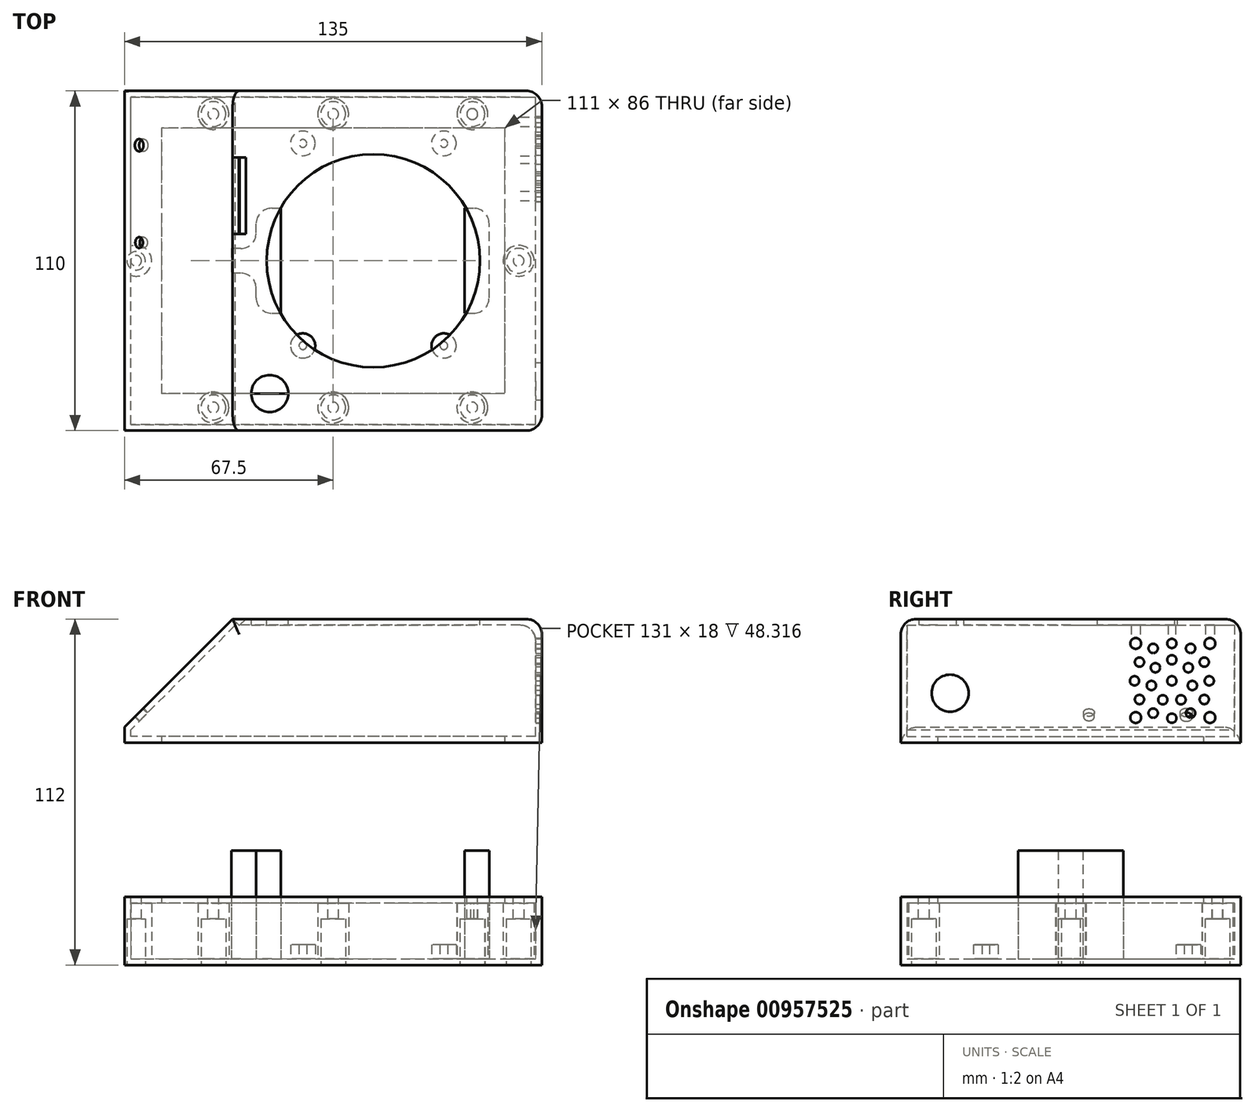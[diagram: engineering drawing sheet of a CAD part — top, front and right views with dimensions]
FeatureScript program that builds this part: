
annotation { "Feature Type Name" : "Feature", "Feature Type Description" : "" }
export const myFeature = defineFeature(function(context is Context, id is Id, definition is map)
    precondition{}
    {
        {
            var Q0;
            Q0=qCreatedBy(makeId("Front.planeOp"),FACE);
            var sketch = newSketch(context, id + "F0", { "sketchPlane" : qUnion([Q0])});
            skLineSegment(sketch, "E0.bottom", {"start": v(67.5, 0) * mm, "end": v(65.5, 0) * mm});
            skLineSegment(sketch, "E0.top", {"start": v(67.5, 40) * mm, "end": v(-32.5, 40) * mm});
            skLineSegment(sketch, "E0.left", {"start": v(67.5, 0) * mm, "end": v(67.5, 40) * mm});
            skLineSegment(sketch, "E0.right", {"start": v(-67.5, 0) * mm, "end": v(-67.5, 5) * mm});
            skLineSegment(sketch, "E1", {"start": v(-32.5, 40) * mm, "end": v(-67.5, 5) * mm});
            skLineSegment(sketch, "E2.0", {"start": v(65.5, 2) * mm, "end": v(65.5, 38) * mm});
            skLineSegment(sketch, "E2.1", {"start": v(65.5, 38) * mm, "end": v(-31.67, 38) * mm});
            skLineSegment(sketch, "E2.2", {"start": v(-31.67, 38) * mm, "end": v(-65.5, 4.17) * mm});
            skLineSegment(sketch, "E2.3", {"start": v(-65.5, 2) * mm, "end": v(-65.5, 4.17) * mm});
            skLineSegment(sketch, "E3.trimOffspring", {"start": v(-65.5, 0) * mm, "end": v(-67.5, 0) * mm});
            skLineSegment(sketch, "E4.bottom", {"start": v(-65.5, 0) * mm, "end": v(-55.5, 0) * mm});
            skLineSegment(sketch, "E4.top", {"start": v(-65.5, 2) * mm, "end": v(-55.5, 2) * mm});
            skLineSegment(sketch, "E4.right", {"start": v(-55.5, 0) * mm, "end": v(-55.5, 2) * mm});
            skLineSegment(sketch, "E5.bottom", {"start": v(65.5, 0) * mm, "end": v(55.5, 0) * mm});
            skLineSegment(sketch, "E5.top", {"start": v(65.5, 2) * mm, "end": v(55.5, 2) * mm});
            skLineSegment(sketch, "E5.right", {"start": v(55.5, 0) * mm, "end": v(55.5, 2) * mm});
            skSolve(sketch);
        }
        {
            var Q0;
            Q0=makeQuery(id+"F0.imprint","IMPRINT",FACE,{"disambiguationData":[TD([[makeQuery(id+"F0.imprint","IMPRINT",EDGE,{"derivedFrom":sQuery(id+"F0.wireOp",EDGE,"E0.bottom")}),-1.0]])]});
            extrude(context, id + "F1", {"entities" : qUnion([Q0]), "depth" : 55 * mm, "offsetDistance" : 25 * mm, "hasSecondDirection" : true, "secondDirectionOppositeDirection" : true, "secondDirectionDepth" : 55 * mm});
        }
        {
            var Q0;
            Q0=makeQuery(id+"F1.opExtrude","SWEPT_FACE",FACE,{"disambiguationData":[OSD([sQuery(id+"F0.wireOp",EDGE,"E0.top")])]});
            var sketch = newSketch(context, id + "F2", { "sketchPlane" : qUnion([Q0])});
            skCircle(sketch, "E6", {"center": v(13, 0) * mm, "radius": 34.5 * mm});
            skCircle(sketch, "E7", {"center": v(-20.5, -43) * mm, "radius": 6 * mm});
            skSolve(sketch);
        }
        {
            var Q0;
            Q0 = qSketchRegion(id + "F2", true);
            extrude(context, id + "F3", {"entities" : qUnion([Q0]), "operationType" : NewBodyOperationType.REMOVE, "oppositeDirection" : true, "depth" : 3 * mm, "offsetDistance" : 25 * mm});
        }
        {
            var Q0;
            Q0=makeQuery(id+"F1.opExtrude","CAP_FACE",FACE,{"disambiguationData":[OSD([sQuery(id+"F0.wireOp",EDGE,"E0.bottom"),sQuery(id+"F0.wireOp",EDGE,"E0.top"),sQuery(id+"F0.wireOp",EDGE,"E0.left"),sQuery(id+"F0.wireOp",EDGE,"E0.right"),sQuery(id+"F0.wireOp",EDGE,"E1"),sQuery(id+"F0.wireOp",EDGE,"E2.0"),sQuery(id+"F0.wireOp",EDGE,"E2.1"),sQuery(id+"F0.wireOp",EDGE,"E2.2"),sQuery(id+"F0.wireOp",EDGE,"E2.3"),sQuery(id+"F0.wireOp",EDGE,"E3.trimOffspring"),sQuery(id+"F0.wireOp",EDGE,"E4.bottom"),sQuery(id+"F0.wireOp",EDGE,"E4.top"),sQuery(id+"F0.wireOp",EDGE,"E4.right"),sQuery(id+"F0.wireOp",EDGE,"E5.bottom"),sQuery(id+"F0.wireOp",EDGE,"E5.top"),sQuery(id+"F0.wireOp",EDGE,"E5.right")])],"isStart":false});
            var sketch = newSketch(context, id + "F4", { "sketchPlane" : qUnion([Q0])});
            skLineSegment(sketch, "E8.0", {"start": v(55.5, 0) * mm, "end": v(55.5, 2) * mm});
            skLineSegment(sketch, "E8.1", {"start": v(65.5, 2) * mm, "end": v(55.5, 2) * mm});
            skLineSegment(sketch, "E8.2", {"start": v(65.5, 2) * mm, "end": v(65.5, 38) * mm});
            skLineSegment(sketch, "E8.3", {"start": v(65.5, 38) * mm, "end": v(-31.67, 38) * mm});
            skLineSegment(sketch, "E8.4", {"start": v(-31.67, 38) * mm, "end": v(-65.5, 4.17) * mm});
            skLineSegment(sketch, "E8.5", {"start": v(-55.5, 0) * mm, "end": v(-55.5, 2) * mm});
            skLineSegment(sketch, "E8.6", {"start": v(-65.5, 2) * mm, "end": v(-55.5, 2) * mm});
            skLineSegment(sketch, "E8.7", {"start": v(-65.5, 2) * mm, "end": v(-65.5, 4.17) * mm});
            skLineSegment(sketch, "E9", {"start": v(-55.5, 0) * mm, "end": v(55.5, 0) * mm});
            skSolve(sketch);
        }
        {
            var Q0;
            Q0 = qSketchRegion(id + "F4", true);
            extrude(context, id + "F5", {"entities" : qUnion([Q0]), "operationType" : NewBodyOperationType.ADD, "oppositeDirection" : true, "depth" : 2 * mm, "offsetDistance" : 25 * mm});
        }
        {
            var Q0;
            Q0=makeQuery(id+"F4.imprint","IMPRINT",FACE,{"disambiguationData":[TD([[makeQuery(id+"F4.imprint","IMPRINT",EDGE,{"derivedFrom":sQuery(id+"F4.wireOp",EDGE,"E8.0")}),1.0]])]});
            extrude(context, id + "F6", {"entities" : qUnion([Q0]), "operationType" : NewBodyOperationType.ADD, "oppositeDirection" : true, "depth" : 2 * mm, "offsetDistance" : 25 * mm});
        }
        {
            var Q0;
            Q0=makeQuery(id+"F1.opExtrude","CAP_FACE",FACE,{"disambiguationData":[OSD([sQuery(id+"F0.wireOp",EDGE,"E0.bottom"),sQuery(id+"F0.wireOp",EDGE,"E0.top"),sQuery(id+"F0.wireOp",EDGE,"E0.left"),sQuery(id+"F0.wireOp",EDGE,"E0.right"),sQuery(id+"F0.wireOp",EDGE,"E1"),sQuery(id+"F0.wireOp",EDGE,"E2.0"),sQuery(id+"F0.wireOp",EDGE,"E2.1"),sQuery(id+"F0.wireOp",EDGE,"E2.2"),sQuery(id+"F0.wireOp",EDGE,"E2.3"),sQuery(id+"F0.wireOp",EDGE,"E3.trimOffspring"),sQuery(id+"F0.wireOp",EDGE,"E4.bottom"),sQuery(id+"F0.wireOp",EDGE,"E4.top"),sQuery(id+"F0.wireOp",EDGE,"E4.right"),sQuery(id+"F0.wireOp",EDGE,"E5.bottom"),sQuery(id+"F0.wireOp",EDGE,"E5.top"),sQuery(id+"F0.wireOp",EDGE,"E5.right")])],"isStart":true});
            var sketch = newSketch(context, id + "F7", { "sketchPlane" : qUnion([Q0])});
            skLineSegment(sketch, "E10.0.0", {"start": v(55.5, 0) * mm, "end": v(55.5, 2) * mm});
            skLineSegment(sketch, "E10.0.1", {"start": v(55.5, 2) * mm, "end": v(65.5, 2) * mm});
            skLineSegment(sketch, "E10.0.2", {"start": v(65.5, 2) * mm, "end": v(65.5, 4.17) * mm});
            skLineSegment(sketch, "E10.0.3", {"start": v(65.5, 4.17) * mm, "end": v(31.67, 38) * mm});
            skLineSegment(sketch, "E10.0.4", {"start": v(31.67, 38) * mm, "end": v(-65.5, 38) * mm});
            skLineSegment(sketch, "E10.0.5", {"start": v(-65.5, 38) * mm, "end": v(-65.5, 2) * mm});
            skLineSegment(sketch, "E10.0.6", {"start": v(-65.5, 2) * mm, "end": v(-55.5, 2) * mm});
            skLineSegment(sketch, "E10.0.7", {"start": v(-55.5, 2) * mm, "end": v(-55.5, 0) * mm});
            skLineSegment(sketch, "E10.0.8", {"start": v(-55.5, 0) * mm, "end": v(55.5, 0) * mm});
            skSolve(sketch);
        }
        {
            var Q0;
            Q0=makeQuery(id+"F7.imprint","IMPRINT",FACE,{"disambiguationData":[TD([[makeQuery(id+"F7.imprint","IMPRINT",EDGE,{"derivedFrom":sQuery(id+"F7.wireOp",EDGE,"E10.0.0")}),1.0]])]});
            extrude(context, id + "F8", {"entities" : qUnion([Q0]), "operationType" : NewBodyOperationType.ADD, "oppositeDirection" : true, "depth" : 2 * mm, "offsetDistance" : 25 * mm});
        }
        {
            var Q0;
            Q0=makeQuery(id+"F1.opExtrude","SWEPT_FACE",FACE,{"disambiguationData":[OSD([sQuery(id+"F0.wireOp",EDGE,"E1")])]});
            var sketch = newSketch(context, id + "F9", { "sketchPlane" : qUnion([Q0])});
            skLineSegment(sketch, "E11.bottom", {"start": v(-8.7, 35.7) * mm, "end": v(-33.5, 35.7) * mm});
            skLineSegment(sketch, "E11.top", {"start": v(-8.7, -35.7) * mm, "end": v(-33.5, -35.7) * mm});
            skLineSegment(sketch, "E11.left", {"start": v(-8.7, 35.7) * mm, "end": v(-8.7, -35.7) * mm});
            skLineSegment(sketch, "E11.right", {"start": v(-33.5, 35.7) * mm, "end": v(-33.5, -35.7) * mm});
            skLineSegment(sketch, "E12.bottom", {"start": v(-5.9, 37.5) * mm, "end": v(-37.4, 37.5) * mm, "construction": true});
            skLineSegment(sketch, "E12.top", {"start": v(-5.9, -37.5) * mm, "end": v(-37.4, -37.5) * mm, "construction": true});
            skLineSegment(sketch, "E12.left", {"start": v(-5.9, 37.5) * mm, "end": v(-5.9, -37.5) * mm, "construction": true});
            skLineSegment(sketch, "E12.right", {"start": v(-37.4, 37.5) * mm, "end": v(-37.4, -37.5) * mm, "construction": true});
            skCircle(sketch, "E13", {"center": v(-37.4, -37.5) * mm, "radius": 2 * mm});
            skCircle(sketch, "E14", {"center": v(-37.4, 37.5) * mm, "radius": 2 * mm});
            skCircle(sketch, "E15", {"center": v(-5.9, 37.5) * mm, "radius": 1.75 * mm});
            skCircle(sketch, "E16", {"center": v(-5.9, -37.5) * mm, "radius": 1.75 * mm});
            skSolve(sketch);
        }
        {
            var Q0;
            Q0=makeQuery(id+"F9.imprint","IMPRINT",FACE,{"disambiguationData":[TD([[makeQuery(id+"F9.imprint","IMPRINT",EDGE,{"derivedFrom":sQuery(id+"F9.wireOp",EDGE,"E11.bottom")}),1.0]])]});
            var Q1;
            Q1=makeQuery(id+"F9.imprint","IMPRINT",FACE,{"disambiguationData":[TD([[makeQuery(id+"F9.imprint","IMPRINT",EDGE,{"derivedFrom":sQuery(id+"F9.wireOp",EDGE,"E15")}),1.0]])]});
            var Q2;
            Q2=makeQuery(id+"F9.imprint","IMPRINT",FACE,{"disambiguationData":[TD([[makeQuery(id+"F9.imprint","IMPRINT",EDGE,{"derivedFrom":sQuery(id+"F9.wireOp",EDGE,"E14")}),1.0]])]});
            var Q3;
            Q3=makeQuery(id+"F9.imprint","IMPRINT",FACE,{"disambiguationData":[TD([[makeQuery(id+"F9.imprint","IMPRINT",EDGE,{"derivedFrom":sQuery(id+"F9.wireOp",EDGE,"E13")}),1.0]])]});
            var Q4;
            Q4=makeQuery(id+"F9.imprint","IMPRINT",FACE,{"disambiguationData":[TD([[makeQuery(id+"F9.imprint","IMPRINT",EDGE,{"derivedFrom":sQuery(id+"F9.wireOp",EDGE,"E16")}),1.0]])]});
            extrude(context, id + "F10", {"entities" : qUnion([Q0, Q1, Q2, Q3, Q4]), "operationType" : NewBodyOperationType.REMOVE, "oppositeDirection" : true, "depth" : 3 * mm, "offsetDistance" : 25 * mm});
        }
        {
            var Q0;
            Q0=qCreatedBy(makeId("Top.planeOp"),FACE);
            var sketch = newSketch(context, id + "F11", { "sketchPlane" : qUnion([Q0])});
            skLineSegment(sketch, "E17.0", {"start": v(55.5, -53) * mm, "end": v(55.5, -43) * mm});
            skLineSegment(sketch, "E17.1", {"start": v(55.5, 53) * mm, "end": v(-55.5, 53) * mm});
            skLineSegment(sketch, "E17.2", {"start": v(-55.5, -53) * mm, "end": v(-55.5, -43) * mm});
            skLineSegment(sketch, "E17.3", {"start": v(-55.5, -53) * mm, "end": v(55.5, -53) * mm});
            skLineSegment(sketch, "E18", {"start": v(55.5, 43) * mm, "end": v(-55.5, 43) * mm});
            skLineSegment(sketch, "E19", {"start": v(55.5, -43) * mm, "end": v(-55.5, -43) * mm});
            skLineSegment(sketch, "E20.trimOffspring", {"start": v(-55.5, 43) * mm, "end": v(-55.5, 53) * mm});
            skLineSegment(sketch, "E21.trimOffspring", {"start": v(55.5, 43) * mm, "end": v(55.5, 53) * mm});
            skSolve(sketch);
        }
        {
            var Q0;
            Q0=makeQuery(id+"F11.imprint","IMPRINT",FACE,{"disambiguationData":[TD([[makeQuery(id+"F11.imprint","IMPRINT",EDGE,{"derivedFrom":sQuery(id+"F11.wireOp",EDGE,"E17.1")}),1.0]])]});
            var Q1;
            Q1=makeQuery(id+"F11.imprint","IMPRINT",FACE,{"disambiguationData":[TD([[makeQuery(id+"F11.imprint","IMPRINT",EDGE,{"derivedFrom":sQuery(id+"F11.wireOp",EDGE,"E17.0")}),1.0]])]});
            extrude(context, id + "F12", {"entities" : qUnion([Q0, Q1]), "operationType" : NewBodyOperationType.ADD, "depth" : 2 * mm, "offsetDistance" : 25 * mm});
        }
        {
            var Q0;
            Q0=makeQuery(id+"F1.opExtrude","SWEPT_FACE",FACE,{"disambiguationData":[OSD([sQuery(id+"F0.wireOp",EDGE,"E0.left")])]});
            var sketch = newSketch(context, id + "F13", { "sketchPlane" : qUnion([Q0])});
            skCircle(sketch, "E22", {"center": v(-39, 16) * mm, "radius": 6 * mm});
            skPoint(sketch, "E23.centerSnap0", {"position": v(55, 20) * mm});
            skLineSegment(sketch, "E24.bottom", {"start": v(21.03, 32.1) * mm, "end": v(45.03, 32.1) * mm, "construction": true});
            skLineSegment(sketch, "E24.top", {"start": v(21.03, 8.1) * mm, "end": v(45.03, 8.1) * mm, "construction": true});
            skLineSegment(sketch, "E24.left", {"start": v(21.03, 32.1) * mm, "end": v(21.03, 8.1) * mm, "construction": true});
            skLineSegment(sketch, "E24.right", {"start": v(45.03, 32.1) * mm, "end": v(45.03, 8.1) * mm, "construction": true});
            skCircle(sketch, "E25", {"center": v(21.03, 32.1) * mm, "radius": 1.75 * mm});
            skCircle(sketch, "E26", {"center": v(45.03, 32.1) * mm, "radius": 1.75 * mm});
            skCircle(sketch, "E27", {"center": v(45.03, 8.1) * mm, "radius": 1.75 * mm});
            skCircle(sketch, "E28", {"center": v(21.03, 8.1) * mm, "radius": 1.75 * mm});
            skPoint(sketch, "E29.center.orphan", {"position": v(45.03, 27.1) * mm});
            skCircle(sketch, "E30", {"center": v(32.73, 20) * mm, "radius": 14.2 * mm, "construction": true});
            skCircle(sketch, "E31.cCircle", {"center": v(32.73, 20) * mm, "radius": 12.1 * mm, "construction": true});
            skLineSegment(sketch, "E31.0", {"start": v(32.73, 32.1) * mm, "end": v(38.78, 30.48) * mm, "construction": true});
            skLineSegment(sketch, "E31.1", {"start": v(38.78, 30.48) * mm, "end": v(43.2, 26.05) * mm, "construction": true});
            skLineSegment(sketch, "E31.2", {"start": v(43.2, 26.05) * mm, "end": v(44.83, 20) * mm, "construction": true});
            skLineSegment(sketch, "E31.3", {"start": v(44.83, 20) * mm, "end": v(43.2, 13.95) * mm, "construction": true});
            skLineSegment(sketch, "E31.4", {"start": v(43.2, 13.95) * mm, "end": v(38.78, 9.52) * mm, "construction": true});
            skLineSegment(sketch, "E31.5", {"start": v(38.78, 9.52) * mm, "end": v(32.73, 7.9) * mm, "construction": true});
            skLineSegment(sketch, "E31.6", {"start": v(32.73, 7.9) * mm, "end": v(26.68, 9.52) * mm, "construction": true});
            skLineSegment(sketch, "E31.7", {"start": v(26.68, 9.52) * mm, "end": v(22.25, 13.95) * mm, "construction": true});
            skLineSegment(sketch, "E31.8", {"start": v(22.25, 13.95) * mm, "end": v(20.63, 20) * mm, "construction": true});
            skLineSegment(sketch, "E31.9", {"start": v(20.63, 20) * mm, "end": v(22.25, 26.05) * mm, "construction": true});
            skLineSegment(sketch, "E31.10", {"start": v(22.25, 26.05) * mm, "end": v(26.68, 30.48) * mm, "construction": true});
            skLineSegment(sketch, "E31.11", {"start": v(26.68, 30.48) * mm, "end": v(32.73, 32.1) * mm, "construction": true});
            skCircle(sketch, "E32", {"center": v(32.73, 32.1) * mm, "radius": 1.5 * mm});
            skCircle(sketch, "E33", {"center": v(38.78, 30.48) * mm, "radius": 1.5 * mm});
            skCircle(sketch, "E34", {"center": v(43.2, 26.05) * mm, "radius": 1.5 * mm});
            skCircle(sketch, "E35", {"center": v(26.68, 30.48) * mm, "radius": 1.5 * mm});
            skCircle(sketch, "E36", {"center": v(22.25, 26.05) * mm, "radius": 1.5 * mm});
            skCircle(sketch, "E37", {"center": v(44.83, 20) * mm, "radius": 1.5 * mm});
            skCircle(sketch, "E38", {"center": v(43.2, 13.95) * mm, "radius": 1.5 * mm});
            skCircle(sketch, "E39", {"center": v(38.78, 9.52) * mm, "radius": 1.5 * mm});
            skCircle(sketch, "E40", {"center": v(32.73, 7.9) * mm, "radius": 1.5 * mm});
            skCircle(sketch, "E41", {"center": v(26.68, 9.52) * mm, "radius": 1.5 * mm});
            skCircle(sketch, "E42", {"center": v(22.25, 13.95) * mm, "radius": 1.5 * mm});
            skCircle(sketch, "E43", {"center": v(20.63, 20) * mm, "radius": 1.5 * mm});
            skCircle(sketch, "E44.cCircle", {"center": v(32.73, 20) * mm, "radius": 6.8 * mm, "construction": true});
            skLineSegment(sketch, "E44.0", {"start": v(32.73, 26.8) * mm, "end": v(38.04, 24.24) * mm, "construction": true});
            skLineSegment(sketch, "E44.1", {"start": v(38.04, 24.24) * mm, "end": v(39.36, 18.49) * mm, "construction": true});
            skLineSegment(sketch, "E44.2", {"start": v(39.36, 18.49) * mm, "end": v(35.68, 13.87) * mm, "construction": true});
            skLineSegment(sketch, "E44.3", {"start": v(35.68, 13.87) * mm, "end": v(29.78, 13.87) * mm, "construction": true});
            skLineSegment(sketch, "E44.4", {"start": v(29.78, 13.87) * mm, "end": v(26.1, 18.49) * mm, "construction": true});
            skLineSegment(sketch, "E44.5", {"start": v(26.1, 18.49) * mm, "end": v(27.41, 24.24) * mm, "construction": true});
            skLineSegment(sketch, "E44.6", {"start": v(27.41, 24.24) * mm, "end": v(32.73, 26.8) * mm, "construction": true});
            skCircle(sketch, "E45", {"center": v(32.73, 26.8) * mm, "radius": 1.5 * mm});
            skCircle(sketch, "E46", {"center": v(38.04, 24.24) * mm, "radius": 1.5 * mm});
            skCircle(sketch, "E47", {"center": v(39.36, 18.49) * mm, "radius": 1.5 * mm});
            skCircle(sketch, "E48", {"center": v(35.68, 13.87) * mm, "radius": 1.5 * mm});
            skCircle(sketch, "E49", {"center": v(29.78, 13.87) * mm, "radius": 1.5 * mm});
            skCircle(sketch, "E50", {"center": v(26.1, 18.49) * mm, "radius": 1.5 * mm});
            skCircle(sketch, "E51", {"center": v(27.41, 24.24) * mm, "radius": 1.5 * mm});
            skCircle(sketch, "E52", {"center": v(32.73, 20) * mm, "radius": 1.5 * mm});
            skSolve(sketch);
        }
        {
            var Q0;
            Q0=makeQuery(id+"F13.imprint","IMPRINT",FACE,{"disambiguationData":[TD([[makeQuery(id+"F13.imprint","IMPRINT",EDGE,{"derivedFrom":sQuery(id+"F13.wireOp",EDGE,"E22")}),1.0]])]});
            var Q1;
            Q1=makeQuery(id+"F13.imprint","IMPRINT",FACE,{"disambiguationData":[TD([[makeQuery(id+"F13.imprint","IMPRINT",EDGE,{"derivedFrom":sQuery(id+"F13.wireOp",EDGE,"E28")}),1.0]])]});
            var Q2;
            Q2=makeQuery(id+"F13.imprint","IMPRINT",FACE,{"disambiguationData":[TD([[makeQuery(id+"F13.imprint","IMPRINT",EDGE,{"derivedFrom":sQuery(id+"F13.wireOp",EDGE,"E41")}),1.0]])]});
            var Q3;
            Q3=makeQuery(id+"F13.imprint","IMPRINT",FACE,{"disambiguationData":[TD([[makeQuery(id+"F13.imprint","IMPRINT",EDGE,{"derivedFrom":sQuery(id+"F13.wireOp",EDGE,"E42")}),1.0]])]});
            var Q4;
            Q4=makeQuery(id+"F13.imprint","IMPRINT",FACE,{"disambiguationData":[TD([[makeQuery(id+"F13.imprint","IMPRINT",EDGE,{"derivedFrom":sQuery(id+"F13.wireOp",EDGE,"E43")}),1.0]])]});
            var Q5;
            Q5=makeQuery(id+"F13.imprint","IMPRINT",FACE,{"disambiguationData":[TD([[makeQuery(id+"F13.imprint","IMPRINT",EDGE,{"derivedFrom":sQuery(id+"F13.wireOp",EDGE,"E50")}),1.0]])]});
            var Q6;
            Q6=makeQuery(id+"F13.imprint","IMPRINT",FACE,{"disambiguationData":[TD([[makeQuery(id+"F13.imprint","IMPRINT",EDGE,{"derivedFrom":sQuery(id+"F13.wireOp",EDGE,"E51")}),1.0]])]});
            var Q7;
            Q7=makeQuery(id+"F13.imprint","IMPRINT",FACE,{"disambiguationData":[TD([[makeQuery(id+"F13.imprint","IMPRINT",EDGE,{"derivedFrom":sQuery(id+"F13.wireOp",EDGE,"E36")}),1.0]])]});
            var Q8;
            Q8=makeQuery(id+"F13.imprint","IMPRINT",FACE,{"disambiguationData":[TD([[makeQuery(id+"F13.imprint","IMPRINT",EDGE,{"derivedFrom":sQuery(id+"F13.wireOp",EDGE,"E35")}),1.0]])]});
            var Q9;
            Q9=makeQuery(id+"F13.imprint","IMPRINT",FACE,{"disambiguationData":[TD([[makeQuery(id+"F13.imprint","IMPRINT",EDGE,{"derivedFrom":sQuery(id+"F13.wireOp",EDGE,"E32")}),1.0]])]});
            var Q10;
            Q10=makeQuery(id+"F13.imprint","IMPRINT",FACE,{"disambiguationData":[TD([[makeQuery(id+"F13.imprint","IMPRINT",EDGE,{"derivedFrom":sQuery(id+"F13.wireOp",EDGE,"E25")}),1.0]])]});
            var Q11;
            Q11=makeQuery(id+"F13.imprint","IMPRINT",FACE,{"disambiguationData":[TD([[makeQuery(id+"F13.imprint","IMPRINT",EDGE,{"derivedFrom":sQuery(id+"F13.wireOp",EDGE,"E33")}),1.0]])]});
            var Q12;
            Q12=makeQuery(id+"F13.imprint","IMPRINT",FACE,{"disambiguationData":[TD([[makeQuery(id+"F13.imprint","IMPRINT",EDGE,{"derivedFrom":sQuery(id+"F13.wireOp",EDGE,"E45")}),1.0]])]});
            var Q13;
            Q13=makeQuery(id+"F13.imprint","IMPRINT",FACE,{"disambiguationData":[TD([[makeQuery(id+"F13.imprint","IMPRINT",EDGE,{"derivedFrom":sQuery(id+"F13.wireOp",EDGE,"E52")}),1.0]])]});
            var Q14;
            Q14=makeQuery(id+"F13.imprint","IMPRINT",FACE,{"disambiguationData":[TD([[makeQuery(id+"F13.imprint","IMPRINT",EDGE,{"derivedFrom":sQuery(id+"F13.wireOp",EDGE,"E48")}),1.0]])]});
            var Q15;
            Q15=makeQuery(id+"F13.imprint","IMPRINT",FACE,{"disambiguationData":[TD([[makeQuery(id+"F13.imprint","IMPRINT",EDGE,{"derivedFrom":sQuery(id+"F13.wireOp",EDGE,"E47")}),1.0]])]});
            var Q16;
            Q16=makeQuery(id+"F13.imprint","IMPRINT",FACE,{"disambiguationData":[TD([[makeQuery(id+"F13.imprint","IMPRINT",EDGE,{"derivedFrom":sQuery(id+"F13.wireOp",EDGE,"E46")}),1.0]])]});
            var Q17;
            Q17=makeQuery(id+"F13.imprint","IMPRINT",FACE,{"disambiguationData":[TD([[makeQuery(id+"F13.imprint","IMPRINT",EDGE,{"derivedFrom":sQuery(id+"F13.wireOp",EDGE,"E34")}),1.0]])]});
            var Q18;
            Q18=makeQuery(id+"F13.imprint","IMPRINT",FACE,{"disambiguationData":[TD([[makeQuery(id+"F13.imprint","IMPRINT",EDGE,{"derivedFrom":sQuery(id+"F13.wireOp",EDGE,"E26")}),1.0]])]});
            var Q19;
            Q19=makeQuery(id+"F13.imprint","IMPRINT",FACE,{"disambiguationData":[TD([[makeQuery(id+"F13.imprint","IMPRINT",EDGE,{"derivedFrom":sQuery(id+"F13.wireOp",EDGE,"E37")}),1.0]])]});
            var Q20;
            Q20=makeQuery(id+"F13.imprint","IMPRINT",FACE,{"disambiguationData":[TD([[makeQuery(id+"F13.imprint","IMPRINT",EDGE,{"derivedFrom":sQuery(id+"F13.wireOp",EDGE,"E38")}),1.0]])]});
            var Q21;
            Q21=makeQuery(id+"F13.imprint","IMPRINT",FACE,{"disambiguationData":[TD([[makeQuery(id+"F13.imprint","IMPRINT",EDGE,{"derivedFrom":sQuery(id+"F13.wireOp",EDGE,"E27")}),1.0]])]});
            var Q22;
            Q22=makeQuery(id+"F13.imprint","IMPRINT",FACE,{"disambiguationData":[TD([[makeQuery(id+"F13.imprint","IMPRINT",EDGE,{"derivedFrom":sQuery(id+"F13.wireOp",EDGE,"E39")}),1.0]])]});
            var Q23;
            Q23=makeQuery(id+"F13.imprint","IMPRINT",FACE,{"disambiguationData":[TD([[makeQuery(id+"F13.imprint","IMPRINT",EDGE,{"derivedFrom":sQuery(id+"F13.wireOp",EDGE,"E40")}),1.0]])]});
            var Q24;
            Q24=makeQuery(id+"F13.imprint","IMPRINT",FACE,{"disambiguationData":[TD([[makeQuery(id+"F13.imprint","IMPRINT",EDGE,{"derivedFrom":sQuery(id+"F13.wireOp",EDGE,"E49")}),1.0]])]});
            extrude(context, id + "F14", {"entities" : qUnion([Q0, Q1, Q2, Q3, Q4, Q5, Q6, Q7, Q8, Q9, Q10, Q11, Q12, Q13, Q14, Q15, Q16, Q17, Q18, Q19, Q20, Q21, Q22, Q23, Q24]), "operationType" : NewBodyOperationType.REMOVE, "oppositeDirection" : true, "depth" : 3 * mm, "offsetDistance" : 25 * mm});
        }
        {
            var Q0;
            Q0=makeQuery(id+"F12.boolean.opBoolean","MERGE",FACE,{"derivedFrom":[makeQuery(id+"F8.boolean.opBoolean","MERGE",FACE,{"derivedFrom":[makeQuery(id+"F5.boolean.opBoolean","MERGE",FACE,{"derivedFrom":[makeQuery(id+"F1.opExtrude","SWEPT_FACE",FACE,{"disambiguationData":[OSD([sQuery(id+"F0.wireOp",EDGE,"E0.bottom"),sQuery(id+"F0.wireOp",EDGE,"E5.bottom")])]}),makeQuery(id+"F1.opExtrude","SWEPT_FACE",FACE,{"disambiguationData":[OSD([sQuery(id+"F0.wireOp",EDGE,"E3.trimOffspring"),sQuery(id+"F0.wireOp",EDGE,"E4.bottom")])]}),makeQuery(id+"F5.opExtrude","SWEPT_FACE",FACE,{"disambiguationData":[OSD([sQuery(id+"F4.wireOp",EDGE,"E9")])]})]}),makeQuery(id+"F8.opExtrude","SWEPT_FACE",FACE,{"disambiguationData":[OSD([sQuery(id+"F7.wireOp",EDGE,"E10.0.8")])]})]}),makeQuery(id+"F12.opExtrude","CAP_FACE",FACE,{"disambiguationData":[OSD([sQuery(id+"F11.wireOp",EDGE,"E17.0"),sQuery(id+"F11.wireOp",EDGE,"E17.2"),sQuery(id+"F11.wireOp",EDGE,"E17.3"),sQuery(id+"F11.wireOp",EDGE,"E19")])],"isStart":true}),makeQuery(id+"F12.opExtrude","CAP_FACE",FACE,{"disambiguationData":[OSD([sQuery(id+"F11.wireOp",EDGE,"E17.1"),sQuery(id+"F11.wireOp",EDGE,"E18"),sQuery(id+"F11.wireOp",EDGE,"E20.trimOffspring"),sQuery(id+"F11.wireOp",EDGE,"E21.trimOffspring")])],"isStart":true})]});
            var sketch = newSketch(context, id + "F15", { "sketchPlane" : qUnion([Q0])});
            skCircle(sketch, "E53", {"center": v(-38.75, 47.5) * mm, "radius": 1.75 * mm});
            skLineSegment(sketch, "E54", {"start": v(-73.28, 47.5) * mm, "end": v(68.94, 47.5) * mm, "construction": true});
            skLineSegment(sketch, "E55", {"start": v(-77.78, -47.5) * mm, "end": v(72.72, -47.5) * mm, "construction": true});
            skLineSegment(sketch, "E56", {"start": v(60, 71.35) * mm, "end": v(60, -59.65) * mm, "construction": true});
            skLineSegment(sketch, "E57", {"start": v(-63.75, 71.72) * mm, "end": v(-63.75, -59.28) * mm, "construction": true});
            skCircle(sketch, "E58", {"center": v(45, 47.5) * mm, "radius": 1.75 * mm});
            skCircle(sketch, "E59", {"center": v(0, 47.5) * mm, "radius": 1.75 * mm});
            skCircle(sketch, "E60", {"center": v(-38.75, -47.5) * mm, "radius": 1.75 * mm});
            skCircle(sketch, "E61", {"center": v(0, -47.5) * mm, "radius": 1.75 * mm});
            skCircle(sketch, "E62", {"center": v(45, -47.5) * mm, "radius": 1.75 * mm});
            skCircle(sketch, "E63", {"center": v(-63.75, 0) * mm, "radius": 1.75 * mm});
            skCircle(sketch, "E64", {"center": v(60, 0) * mm, "radius": 1.75 * mm});
            skSolve(sketch);
        }
        {
            var Q0;
            Q0=makeQuery(id+"F1.opExtrude","CAP_EDGE",EDGE,{"disambiguationData":[OSD([sQuery(id+"F0.wireOp",EDGE,"E0.top")])],"isStart":false});
            var Q1;
            Q1=makeQuery(id+"F5.opExtrude","CAP_EDGE",EDGE,{"disambiguationData":[OSD([sQuery(id+"F4.wireOp",EDGE,"E8.3")])],"isStart":false});
            var Q2;
            Q2=makeQuery(id+"F5.opExtrude","CAP_EDGE",EDGE,{"disambiguationData":[OSD([sQuery(id+"F4.wireOp",EDGE,"E8.4")])],"isStart":false});
            var Q3;
            Q3=makeQuery(id+"F8.opExtrude","CAP_EDGE",EDGE,{"disambiguationData":[OSD([sQuery(id+"F7.wireOp",EDGE,"E10.0.4")])],"isStart":false});
            var Q4;
            Q4=makeQuery(id+"F8.opExtrude","CAP_EDGE",EDGE,{"disambiguationData":[OSD([sQuery(id+"F7.wireOp",EDGE,"E10.0.3")])],"isStart":false});
            var Q5;
            Q5=makeQuery(id+"F1.opExtrude","SWEPT_EDGE",EDGE,{"disambiguationData":[OSD([sQuery(id+"F0.wireOp",EDGE,"E2.0"),sQuery(id+"F0.wireOp",EDGE,"E2.1")])]});
            var Q6;
            Q6=makeQuery(id+"F8.opExtrude","CAP_EDGE",EDGE,{"disambiguationData":[OSD([sQuery(id+"F7.wireOp",EDGE,"E10.0.5")])],"isStart":false});
            var Q7;
            Q7=makeQuery(id+"F5.opExtrude","CAP_EDGE",EDGE,{"disambiguationData":[OSD([sQuery(id+"F4.wireOp",EDGE,"E8.2")])],"isStart":false});
            var Q8;
            Q8=makeQuery(id+"F1.opExtrude","CAP_EDGE",EDGE,{"disambiguationData":[OSD([sQuery(id+"F0.wireOp",EDGE,"E0.left")])],"isStart":true});
            var Q9;
            Q9=makeQuery(id+"F1.opExtrude","SWEPT_EDGE",EDGE,{"disambiguationData":[OSD([sQuery(id+"F0.wireOp",EDGE,"E0.top"),sQuery(id+"F0.wireOp",EDGE,"E0.left")])]});
            var Q10;
            Q10=makeQuery(id+"F1.opExtrude","CAP_EDGE",EDGE,{"disambiguationData":[OSD([sQuery(id+"F0.wireOp",EDGE,"E0.top")])],"isStart":true});
            var Q11;
            Q11=makeQuery(id+"F1.opExtrude","CAP_EDGE",EDGE,{"disambiguationData":[OSD([sQuery(id+"F0.wireOp",EDGE,"E0.left")])],"isStart":false});
            var Q12;
            Q12=makeQuery(id+"F1.opExtrude","CAP_EDGE",EDGE,{"disambiguationData":[OSD([sQuery(id+"F0.wireOp",EDGE,"E1")])],"isStart":false});
            var Q13;
            Q13=makeQuery(id+"F1.opExtrude","CAP_EDGE",EDGE,{"disambiguationData":[OSD([sQuery(id+"F0.wireOp",EDGE,"E1")])],"isStart":true});
            fillet(context, id + "F16", {"entities" : qUnion([Q0, Q1, Q2, Q3, Q4, Q5, Q6, Q7, Q8, Q9, Q10, Q11, Q12, Q13]), "radius" : 5 * mm, "tangentPropagation" : true, "allowEdgeOverflow" : false});
        }
        {
            var Q0;
            Q0=qCreatedBy(makeId("Top.planeOp"),FACE);
            cPlane(context, id + "F17", {"entities" : qUnion([Q0]), "cplaneType" : CPlaneType.OFFSET, "offset" : 70 * mm, "oppositeDirection" : true, "width" : 150 * mm, "height" : 150 * mm});
        }
        {
            var Q0;
            Q0=qCreatedBy(id+"F17.planeOp",FACE);
            var sketch = newSketch(context, id + "F18", { "sketchPlane" : qUnion([Q0])});
            skLineSegment(sketch, "E65.0.0", {"start": v(-67.5, -55) * mm, "end": v(-67.5, 55) * mm});
            skLineSegment(sketch, "E65.0.1", {"start": v(-67.5, 55) * mm, "end": v(67.5, 55) * mm});
            skLineSegment(sketch, "E65.0.2", {"start": v(67.5, 55) * mm, "end": v(67.5, -55) * mm});
            skLineSegment(sketch, "E65.0.3", {"start": v(67.5, -55) * mm, "end": v(-67.5, -55) * mm});
            skCircle(sketch, "E66.0", {"center": v(45.04, 47.49) * mm, "radius": 1.75 * mm});
            skCircle(sketch, "E66.1", {"center": v(0, 47.5) * mm, "radius": 1.75 * mm});
            skCircle(sketch, "E66.3", {"center": v(60, 0) * mm, "radius": 1.75 * mm});
            skCircle(sketch, "E66.4", {"center": v(45, -47.5) * mm, "radius": 1.75 * mm});
            skCircle(sketch, "E66.5", {"center": v(0, -47.5) * mm, "radius": 1.75 * mm});
            skCircle(sketch, "E66.6", {"center": v(-38.75, -47.5) * mm, "radius": 1.75 * mm});
            skCircle(sketch, "E66.7", {"center": v(-63.75, 0) * mm, "radius": 1.75 * mm});
            skCircle(sketch, "E66.8", {"center": v(-38.75, 47.5) * mm, "radius": 1.75 * mm});
            skSolve(sketch);
        }
        {
            var Q0;
            Q0=makeQuery(id+"F18.imprint","IMPRINT",FACE,{"disambiguationData":[TD([[makeQuery(id+"F18.imprint","IMPRINT",EDGE,{"derivedFrom":sQuery(id+"F18.wireOp",EDGE,"E65.0.0")}),-1.0]])]});
            extrude(context, id + "F19", {"entities" : qUnion([Q0]), "oppositeDirection" : true, "depth" : 2 * mm, "offsetDistance" : 25 * mm});
        }
        {
            var Q0;
            Q0=makeQuery(id+"F19.opExtrude","CAP_FACE",FACE,{"disambiguationData":[OSD([sQuery(id+"F18.wireOp",EDGE,"E65.0.0"),sQuery(id+"F18.wireOp",EDGE,"E65.0.1"),sQuery(id+"F18.wireOp",EDGE,"E65.0.2"),sQuery(id+"F18.wireOp",EDGE,"E65.0.3"),sQuery(id+"F18.wireOp",EDGE,"E66.0"),sQuery(id+"F18.wireOp",EDGE,"E66.1"),sQuery(id+"F18.wireOp",EDGE,"E66.3"),sQuery(id+"F18.wireOp",EDGE,"E66.4"),sQuery(id+"F18.wireOp",EDGE,"E66.5"),sQuery(id+"F18.wireOp",EDGE,"E66.6"),sQuery(id+"F18.wireOp",EDGE,"E66.7"),sQuery(id+"F18.wireOp",EDGE,"E66.8")])],"isStart":false});
            var sketch = newSketch(context, id + "F20", { "sketchPlane" : qUnion([Q0])});
            skLineSegment(sketch, "E67.bottom", {"start": v(67.5, -55) * mm, "end": v(-67.5, -55) * mm});
            skLineSegment(sketch, "E67.top", {"start": v(67.5, 55) * mm, "end": v(-67.5, 55) * mm});
            skLineSegment(sketch, "E67.left", {"start": v(67.5, -55) * mm, "end": v(67.5, 55) * mm});
            skLineSegment(sketch, "E67.right", {"start": v(-67.5, -55) * mm, "end": v(-67.5, 55) * mm});
            skLineSegment(sketch, "E68.bottom", {"start": v(65.5, -53) * mm, "end": v(-65.5, -53) * mm});
            skLineSegment(sketch, "E68.top", {"start": v(65.5, 53) * mm, "end": v(-65.5, 53) * mm});
            skLineSegment(sketch, "E68.left", {"start": v(65.5, -53) * mm, "end": v(65.5, 53) * mm});
            skLineSegment(sketch, "E68.right", {"start": v(-65.5, -53) * mm, "end": v(-65.5, -4.68) * mm});
            skCircle(sketch, "E69", {"center": v(-38.75, -47.5) * mm, "radius": 5 * mm});
            skArc(sketch, "E70", {"start": v(-65.5, -4.68) * mm, "mid": v(-58.75, 0) * mm, "end": v(-65.5, 4.68) * mm});
            skCircle(sketch, "E71", {"center": v(-38.75, 47.5) * mm, "radius": 5 * mm});
            skCircle(sketch, "E72", {"center": v(0, 47.5) * mm, "radius": 5 * mm});
            skCircle(sketch, "E73", {"center": v(0, -47.5) * mm, "radius": 5 * mm});
            skCircle(sketch, "E74", {"center": v(45.04, -47.49) * mm, "radius": 5 * mm});
            skCircle(sketch, "E75", {"center": v(45, 47.5) * mm, "radius": 5 * mm});
            skCircle(sketch, "E76", {"center": v(60, 0) * mm, "radius": 5 * mm});
            skLineSegment(sketch, "E77.trimOffspring", {"start": v(-65.5, 4.68) * mm, "end": v(-65.5, 53) * mm});
            skSolve(sketch);
        }
        {
            var Q0;
            Q0=makeQuery(id+"F20.imprint","IMPRINT",FACE,{"disambiguationData":[TD([[makeQuery(id+"F20.imprint","IMPRINT",EDGE,{"derivedFrom":sQuery(id+"F20.wireOp",EDGE,"E67.bottom")}),1.0]])]});
            var Q1;
            Q1=makeQuery(id+"F20.imprint","IMPRINT",FACE,{"disambiguationData":[TD([[makeQuery(id+"F20.imprint","IMPRINT",EDGE,{"derivedFrom":sQuery(id+"F20.wireOp",EDGE,"E69")}),1.0]])]});
            var Q2;
            Q2=makeQuery(id+"F20.imprint","IMPRINT",FACE,{"disambiguationData":[TD([[makeQuery(id+"F20.imprint","IMPRINT",EDGE,{"derivedFrom":sQuery(id+"F20.wireOp",EDGE,"E71")}),1.0]])]});
            var Q3;
            Q3=makeQuery(id+"F20.imprint","IMPRINT",FACE,{"disambiguationData":[TD([[makeQuery(id+"F20.imprint","IMPRINT",EDGE,{"derivedFrom":sQuery(id+"F20.wireOp",EDGE,"E72")}),1.0]])]});
            var Q4;
            Q4=makeQuery(id+"F20.imprint","IMPRINT",FACE,{"disambiguationData":[TD([[makeQuery(id+"F20.imprint","IMPRINT",EDGE,{"derivedFrom":sQuery(id+"F20.wireOp",EDGE,"E73")}),1.0]])]});
            var Q5;
            Q5=makeQuery(id+"F20.imprint","IMPRINT",FACE,{"disambiguationData":[TD([[makeQuery(id+"F20.imprint","IMPRINT",EDGE,{"derivedFrom":sQuery(id+"F20.wireOp",EDGE,"E76")}),1.0]])]});
            var Q6;
            Q6=makeQuery(id+"F20.imprint","IMPRINT",FACE,{"disambiguationData":[TD([[makeQuery(id+"F20.imprint","IMPRINT",EDGE,{"derivedFrom":sQuery(id+"F20.wireOp",EDGE,"E75")}),1.0]])]});
            var Q7;
            Q7=makeQuery(id+"F20.imprint","IMPRINT",FACE,{"disambiguationData":[TD([[makeQuery(id+"F20.imprint","IMPRINT",EDGE,{"derivedFrom":sQuery(id+"F20.wireOp",EDGE,"E74")}),1.0]])]});
            extrude(context, id + "F21", {"entities" : qUnion([Q0, Q1, Q2, Q3, Q4, Q5, Q6, Q7]), "operationType" : NewBodyOperationType.ADD, "oppositeDirection" : true, "depth" : 20 * mm, "offsetDistance" : 25 * mm});
        }
        {
            var Q0;
            Q0=makeQuery(id+"F21.opExtrude","CAP_FACE",FACE,{"disambiguationData":[OSD([sQuery(id+"F20.wireOp",EDGE,"E67.bottom"),sQuery(id+"F20.wireOp",EDGE,"E67.top"),sQuery(id+"F20.wireOp",EDGE,"E67.left"),sQuery(id+"F20.wireOp",EDGE,"E67.right"),sQuery(id+"F20.wireOp",EDGE,"E68.bottom"),sQuery(id+"F20.wireOp",EDGE,"E68.top"),sQuery(id+"F20.wireOp",EDGE,"E68.left"),sQuery(id+"F20.wireOp",EDGE,"E68.right")])],"isStart":false});
            var sketch = newSketch(context, id + "F22", { "sketchPlane" : qUnion([Q0])});
            skLineSegment(sketch, "E78.bottom", {"start": v(67.5, 55) * mm, "end": v(-67.5, 55) * mm});
            skLineSegment(sketch, "E78.top", {"start": v(67.5, -55) * mm, "end": v(-67.5, -55) * mm});
            skLineSegment(sketch, "E78.left", {"start": v(67.5, 55) * mm, "end": v(67.5, -55) * mm});
            skLineSegment(sketch, "E78.right", {"start": v(-67.5, 55) * mm, "end": v(-67.5, -55) * mm});
            skLineSegment(sketch, "E79.bottom", {"start": v(55.5, 43) * mm, "end": v(-55.5, 43) * mm});
            skLineSegment(sketch, "E79.top", {"start": v(55.5, -43) * mm, "end": v(-55.5, -43) * mm});
            skLineSegment(sketch, "E79.left", {"start": v(55.5, 43) * mm, "end": v(55.5, -43) * mm});
            skLineSegment(sketch, "E79.right", {"start": v(-55.5, 43) * mm, "end": v(-55.5, -43) * mm});
            skSolve(sketch);
        }
        {
            var Q0;
            Q0=makeQuery(id+"F22.imprint","IMPRINT",FACE,{"disambiguationData":[TD([[makeQuery(id+"F22.imprint","IMPRINT",EDGE,{"derivedFrom":sQuery(id+"F22.wireOp",EDGE,"E78.bottom")}),-1.0]])]});
            var Q1;
            Q1=makeQuery(id+"F22.imprint","IMPRINT",FACE,{"disambiguationData":[TD([[makeQuery(id+"F22.imprint","IMPRINT",EDGE,{"derivedFrom":sQuery(id+"F22.wireOp",EDGE,"E79.bottom")}),-1.0]])]});
            extrude(context, id + "F23", {"entities" : qUnion([Q0, Q1]), "operationType" : NewBodyOperationType.ADD, "depth" : 2 * mm, "offsetDistance" : 25 * mm});
        }
        {
            var Q0;
            Q0=makeQuery(id+"F23.opExtrude","CAP_FACE",FACE,{"disambiguationData":[OSD([sQuery(id+"F22.wireOp",EDGE,"E78.bottom"),sQuery(id+"F22.wireOp",EDGE,"E78.top"),sQuery(id+"F22.wireOp",EDGE,"E78.left"),sQuery(id+"F22.wireOp",EDGE,"E78.right"),sQuery(id+"F22.wireOp",EDGE,"E79.bottom"),sQuery(id+"F22.wireOp",EDGE,"E79.top"),sQuery(id+"F22.wireOp",EDGE,"E79.left"),sQuery(id+"F22.wireOp",EDGE,"E79.right")])],"isStart":false});
            var sketch = newSketch(context, id + "F24", { "sketchPlane" : qUnion([Q0])});
            skPoint(sketch, "E80.0", {"position": v(-38.75, 47.5) * mm});
            skPoint(sketch, "E80.1", {"position": v(0, 47.5) * mm});
            skPoint(sketch, "E80.2", {"position": v(-63.75, 0) * mm});
            skPoint(sketch, "E80.3", {"position": v(-38.75, -47.5) * mm});
            skPoint(sketch, "E80.4", {"position": v(0, -47.5) * mm});
            skPoint(sketch, "E80.5", {"position": v(45, -47.5) * mm});
            skPoint(sketch, "E80.6", {"position": v(60, 0) * mm});
            skPoint(sketch, "E80.7", {"position": v(45, 47.5) * mm});
            skCircle(sketch, "E81.0", {"center": v(-63.75, 0) * mm, "radius": 1.75 * mm});
            skCircle(sketch, "E81.1", {"center": v(-38.75, -47.5) * mm, "radius": 1.75 * mm});
            skCircle(sketch, "E81.2", {"center": v(-38.75, 47.5) * mm, "radius": 1.75 * mm});
            skCircle(sketch, "E81.3", {"center": v(0, 47.5) * mm, "radius": 1.75 * mm});
            skCircle(sketch, "E81.4", {"center": v(45, 47.5) * mm, "radius": 1.75 * mm});
            skCircle(sketch, "E81.5", {"center": v(60, 0) * mm, "radius": 1.75 * mm});
            skCircle(sketch, "E81.6", {"center": v(45, -47.5) * mm, "radius": 1.75 * mm});
            skCircle(sketch, "E81.7", {"center": v(0, -47.5) * mm, "radius": 1.75 * mm});
            skSolve(sketch);
        }
        {
            var Q0;
            Q0 = qSketchRegion(id + "F24", true);
            extrude(context, id + "F25", {"entities" : qUnion([Q0]), "operationType" : NewBodyOperationType.REMOVE, "oppositeDirection" : true, "depth" : 25 * mm, "offsetDistance" : 25 * mm});
        }
        {
            var Q0;
            Q0=makeQuery(id+"F19.opExtrude","CAP_FACE",FACE,{"disambiguationData":[OSD([sQuery(id+"F18.wireOp",EDGE,"E65.0.0"),sQuery(id+"F18.wireOp",EDGE,"E65.0.1"),sQuery(id+"F18.wireOp",EDGE,"E65.0.2"),sQuery(id+"F18.wireOp",EDGE,"E65.0.3"),sQuery(id+"F18.wireOp",EDGE,"E66.0"),sQuery(id+"F18.wireOp",EDGE,"E66.1"),sQuery(id+"F18.wireOp",EDGE,"E66.3"),sQuery(id+"F18.wireOp",EDGE,"E66.4"),sQuery(id+"F18.wireOp",EDGE,"E66.5"),sQuery(id+"F18.wireOp",EDGE,"E66.6"),sQuery(id+"F18.wireOp",EDGE,"E66.7"),sQuery(id+"F18.wireOp",EDGE,"E66.8")])],"isStart":false});
            var sketch = newSketch(context, id + "F26", { "sketchPlane" : qUnion([Q0])});
            skCircle(sketch, "E82", {"center": v(60, 0) * mm, "radius": 4 * mm});
            skCircle(sketch, "E83", {"center": v(45, 47.5) * mm, "radius": 4 * mm});
            skCircle(sketch, "E84", {"center": v(0, 47.5) * mm, "radius": 4 * mm});
            skCircle(sketch, "E85", {"center": v(-38.75, 47.5) * mm, "radius": 4 * mm});
            skCircle(sketch, "E86", {"center": v(-63.75, 0) * mm, "radius": 3 * mm});
            skCircle(sketch, "E87", {"center": v(-38.75, -47.5) * mm, "radius": 4 * mm});
            skCircle(sketch, "E88", {"center": v(0, -47.5) * mm, "radius": 4 * mm});
            skCircle(sketch, "E89", {"center": v(45.04, -47.49) * mm, "radius": 4 * mm});
            skSolve(sketch);
        }
        {
            var Q0;
            Q0=makeQuery(id+"F26.imprint","IMPRINT",FACE,{"disambiguationData":[TD([[makeQuery(id+"F26.imprint","IMPRINT",EDGE,{"derivedFrom":sQuery(id+"F26.wireOp",EDGE,"E84")}),1.0]])]});
            var Q1;
            Q1=makeQuery(id+"F26.imprint","IMPRINT",FACE,{"disambiguationData":[TD([[makeQuery(id+"F26.imprint","IMPRINT",EDGE,{"derivedFrom":sQuery(id+"F26.wireOp",EDGE,"E83")}),1.0]])]});
            var Q2;
            Q2=makeQuery(id+"F26.imprint","IMPRINT",FACE,{"disambiguationData":[TD([[makeQuery(id+"F26.imprint","IMPRINT",EDGE,{"derivedFrom":sQuery(id+"F26.wireOp",EDGE,"E82")}),1.0]])]});
            var Q3;
            Q3=makeQuery(id+"F26.imprint","IMPRINT",FACE,{"disambiguationData":[TD([[makeQuery(id+"F26.imprint","IMPRINT",EDGE,{"derivedFrom":sQuery(id+"F26.wireOp",EDGE,"E88")}),1.0]])]});
            var Q4;
            Q4=makeQuery(id+"F26.imprint","IMPRINT",FACE,{"disambiguationData":[TD([[makeQuery(id+"F26.imprint","IMPRINT",EDGE,{"derivedFrom":sQuery(id+"F26.wireOp",EDGE,"E89")}),1.0]])]});
            var Q5;
            Q5=makeQuery(id+"F26.imprint","IMPRINT",FACE,{"disambiguationData":[TD([[makeQuery(id+"F26.imprint","IMPRINT",EDGE,{"derivedFrom":sQuery(id+"F26.wireOp",EDGE,"E87")}),1.0]])]});
            var Q6;
            Q6=makeQuery(id+"F26.imprint","IMPRINT",FACE,{"disambiguationData":[TD([[makeQuery(id+"F26.imprint","IMPRINT",EDGE,{"derivedFrom":sQuery(id+"F26.wireOp",EDGE,"E85")}),1.0]])]});
            var Q7;
            Q7=makeQuery(id+"F26.imprint","IMPRINT",FACE,{"disambiguationData":[TD([[makeQuery(id+"F26.imprint","IMPRINT",EDGE,{"derivedFrom":sQuery(id+"F26.wireOp",EDGE,"E86")}),1.0]])]});
            extrude(context, id + "F27", {"entities" : qUnion([Q0, Q1, Q2, Q3, Q4, Q5, Q6, Q7]), "operationType" : NewBodyOperationType.REMOVE, "oppositeDirection" : true, "depth" : 15 * mm, "offsetDistance" : 25 * mm});
        }
        {
            var Q0;
            Q0=makeQuery(id+"F23.boolean.opBoolean","MERGE",EDGE,{"derivedFrom":[makeQuery(id+"F21.boolean.opBoolean","MERGE",EDGE,{"derivedFrom":[makeQuery(id+"F19.opExtrude","SWEPT_EDGE",EDGE,{"disambiguationData":[OSD([sQuery(id+"F18.wireOp",EDGE,"E65.0.2"),sQuery(id+"F18.wireOp",EDGE,"E65.0.3")])]}),makeQuery(id+"F21.opExtrude","SWEPT_EDGE",EDGE,{"disambiguationData":[OSD([sQuery(id+"F20.wireOp",EDGE,"E67.top"),sQuery(id+"F20.wireOp",EDGE,"E67.left")])]})]}),makeQuery(id+"F23.opExtrude","SWEPT_EDGE",EDGE,{"disambiguationData":[OSD([sQuery(id+"F22.wireOp",EDGE,"E78.top"),sQuery(id+"F22.wireOp",EDGE,"E78.left")])]})]});
            var Q1;
            Q1=makeQuery(id+"F23.boolean.opBoolean","MERGE",EDGE,{"derivedFrom":[makeQuery(id+"F21.boolean.opBoolean","MERGE",EDGE,{"derivedFrom":[makeQuery(id+"F19.opExtrude","SWEPT_EDGE",EDGE,{"disambiguationData":[OSD([sQuery(id+"F18.wireOp",EDGE,"E65.0.1"),sQuery(id+"F18.wireOp",EDGE,"E65.0.2")])]}),makeQuery(id+"F21.opExtrude","SWEPT_EDGE",EDGE,{"disambiguationData":[OSD([sQuery(id+"F20.wireOp",EDGE,"E67.bottom"),sQuery(id+"F20.wireOp",EDGE,"E67.left")])]})]}),makeQuery(id+"F23.opExtrude","SWEPT_EDGE",EDGE,{"disambiguationData":[OSD([sQuery(id+"F22.wireOp",EDGE,"E78.bottom"),sQuery(id+"F22.wireOp",EDGE,"E78.left")])]})]});
            fillet(context, id + "F28", {"entities" : qUnion([Q0, Q1]), "radius" : 5 * mm, "tangentPropagation" : true, "allowEdgeOverflow" : false});
        }
        {
            var Q0;
            Q0=makeQuery(id+"F19.opExtrude","CAP_FACE",FACE,{"disambiguationData":[OSD([sQuery(id+"F18.wireOp",EDGE,"E65.0.0"),sQuery(id+"F18.wireOp",EDGE,"E65.0.1"),sQuery(id+"F18.wireOp",EDGE,"E65.0.2"),sQuery(id+"F18.wireOp",EDGE,"E65.0.3"),sQuery(id+"F18.wireOp",EDGE,"E66.0"),sQuery(id+"F18.wireOp",EDGE,"E66.1"),sQuery(id+"F18.wireOp",EDGE,"E66.3"),sQuery(id+"F18.wireOp",EDGE,"E66.4"),sQuery(id+"F18.wireOp",EDGE,"E66.5"),sQuery(id+"F18.wireOp",EDGE,"E66.6"),sQuery(id+"F18.wireOp",EDGE,"E66.7"),sQuery(id+"F18.wireOp",EDGE,"E66.8")])],"isStart":true});
            var sketch = newSketch(context, id + "F29", { "sketchPlane" : qUnion([Q0])});
            skLineSegment(sketch, "E90.bottom", {"start": v(35.8, -27.5) * mm, "end": v(-9.8, -27.5) * mm, "construction": true});
            skLineSegment(sketch, "E90.top", {"start": v(35.8, 38) * mm, "end": v(-9.8, 38) * mm, "construction": true});
            skLineSegment(sketch, "E90.left", {"start": v(35.8, -27.5) * mm, "end": v(35.8, 38) * mm, "construction": true});
            skLineSegment(sketch, "E90.right", {"start": v(-9.8, -27.5) * mm, "end": v(-9.8, 38) * mm, "construction": true});
            skCircle(sketch, "E91", {"center": v(-9.8, 38) * mm, "radius": 4 * mm});
            skCircle(sketch, "E92", {"center": v(35.8, 38) * mm, "radius": 4 * mm});
            skCircle(sketch, "E93", {"center": v(35.8, -27.5) * mm, "radius": 4 * mm});
            skCircle(sketch, "E94", {"center": v(-9.8, -27.5) * mm, "radius": 4 * mm});
            skCircle(sketch, "E95", {"center": v(-9.8, 38) * mm, "radius": 1.25 * mm});
            skCircle(sketch, "E96", {"center": v(35.8, 38) * mm, "radius": 1.25 * mm});
            skCircle(sketch, "E97", {"center": v(35.8, -27.5) * mm, "radius": 1.25 * mm});
            skCircle(sketch, "E98", {"center": v(-9.8, -27.5) * mm, "radius": 1.25 * mm});
            skSolve(sketch);
        }
        {
            var Q0;
            Q0 = qSketchRegion(id + "F29", true);
            var Q1;
            Q1=sQuery(id+"F29.wireOp",EDGE,"E91");
            extrude(context, id + "F30", {"entities" : qUnion([Q0]), "operationType" : NewBodyOperationType.ADD, "surfaceOperationType" : NewSurfaceOperationType.ADD, "surfaceEntities" : qUnion([Q1]), "depth" : 4.5 * mm, "offsetDistance" : 25 * mm});
        }
        {
            var Q0;
            Q0=makeQuery(id+"F30.boolean.opBoolean","SPLIT",FACE,{"disambiguationData":[TD([makeQuery(id+"F21.opExtrude","SWEPT_FACE",FACE,{"disambiguationData":[OSD([sQuery(id+"F20.wireOp",EDGE,"E68.bottom")])]})])],"derivedFrom":makeQuery(id+"F19.opExtrude","CAP_FACE",FACE,{"disambiguationData":[OSD([sQuery(id+"F18.wireOp",EDGE,"E65.0.0"),sQuery(id+"F18.wireOp",EDGE,"E65.0.1"),sQuery(id+"F18.wireOp",EDGE,"E65.0.2"),sQuery(id+"F18.wireOp",EDGE,"E65.0.3"),sQuery(id+"F18.wireOp",EDGE,"E66.0"),sQuery(id+"F18.wireOp",EDGE,"E66.1"),sQuery(id+"F18.wireOp",EDGE,"E66.3"),sQuery(id+"F18.wireOp",EDGE,"E66.4"),sQuery(id+"F18.wireOp",EDGE,"E66.5"),sQuery(id+"F18.wireOp",EDGE,"E66.6"),sQuery(id+"F18.wireOp",EDGE,"E66.7"),sQuery(id+"F18.wireOp",EDGE,"E66.8")])],"isStart":true})});
            var sketch = newSketch(context, id + "F31", { "sketchPlane" : qUnion([Q0])});
            skLineSegment(sketch, "E99.bottom", {"start": v(-24.9, -17) * mm, "end": v(-16.9, -17) * mm});
            skLineSegment(sketch, "E99.top", {"start": v(-24.9, 17) * mm, "end": v(-16.9, 17) * mm});
            skLineSegment(sketch, "E99.left", {"start": v(-24.9, -17) * mm, "end": v(-24.9, -4) * mm});
            skLineSegment(sketch, "E99.right", {"start": v(-16.9, -17) * mm, "end": v(-16.9, 17) * mm});
            skLineSegment(sketch, "E100.bottom", {"start": v(-24.9, 4) * mm, "end": v(-32.9, 4) * mm});
            skLineSegment(sketch, "E100.top", {"start": v(-24.9, -4) * mm, "end": v(-32.9, -4) * mm});
            skLineSegment(sketch, "E100.left", {"start": v(-16.9, 4) * mm, "end": v(-16.9, -4) * mm});
            skLineSegment(sketch, "E100.right", {"start": v(-32.9, 4) * mm, "end": v(-32.9, -4) * mm});
            skLineSegment(sketch, "E101.trimOffspring", {"start": v(-24.9, 4) * mm, "end": v(-24.9, 17) * mm});
            skLineSegment(sketch, "E102.bottom", {"start": v(42.45, -17) * mm, "end": v(50.45, -17) * mm});
            skLineSegment(sketch, "E102.top", {"start": v(42.45, 17) * mm, "end": v(50.45, 17) * mm});
            skLineSegment(sketch, "E102.left", {"start": v(42.45, -17) * mm, "end": v(42.45, 17) * mm});
            skLineSegment(sketch, "E102.right", {"start": v(50.45, -17) * mm, "end": v(50.45, 17) * mm});
            skSolve(sketch);
        }
        {
            var Q0;
            Q0 = qSketchRegion(id + "F31", true);
            extrude(context, id + "F32", {"entities" : qUnion([Q0]), "operationType" : NewBodyOperationType.ADD, "depth" : 35 * mm, "offsetDistance" : 25 * mm});
        }
        {
            var Q0;
            Q0=makeQuery(id+"F32.opExtrude","SWEPT_EDGE",EDGE,{"disambiguationData":[OSD([sQuery(id+"F31.wireOp",EDGE,"E99.left"),sQuery(id+"F31.wireOp",EDGE,"E100.top")])]});
            var Q1;
            Q1=makeQuery(id+"F32.opExtrude","SWEPT_EDGE",EDGE,{"disambiguationData":[OSD([sQuery(id+"F31.wireOp",EDGE,"E100.bottom"),sQuery(id+"F31.wireOp",EDGE,"E101.trimOffspring")])]});
            var Q2;
            Q2=makeQuery(id+"F32.opExtrude","SWEPT_EDGE",EDGE,{"disambiguationData":[OSD([sQuery(id+"F31.wireOp",EDGE,"E102.bottom"),sQuery(id+"F31.wireOp",EDGE,"E102.right")])]});
            var Q3;
            Q3=makeQuery(id+"F32.opExtrude","SWEPT_EDGE",EDGE,{"disambiguationData":[OSD([sQuery(id+"F31.wireOp",EDGE,"E102.top"),sQuery(id+"F31.wireOp",EDGE,"E102.right")])]});
            var Q4;
            Q4=makeQuery(id+"F32.opExtrude","SWEPT_EDGE",EDGE,{"disambiguationData":[OSD([sQuery(id+"F31.wireOp",EDGE,"E99.top"),sQuery(id+"F31.wireOp",EDGE,"E101.trimOffspring")])]});
            var Q5;
            Q5=makeQuery(id+"F32.opExtrude","SWEPT_EDGE",EDGE,{"disambiguationData":[OSD([sQuery(id+"F31.wireOp",EDGE,"E99.bottom"),sQuery(id+"F31.wireOp",EDGE,"E99.left")])]});
            fillet(context, id + "F33", {"entities" : qUnion([Q0, Q1, Q2, Q3, Q4, Q5]), "radius" : 5 * mm, "tangentPropagation" : true, "allowEdgeOverflow" : false});
        }
    });
